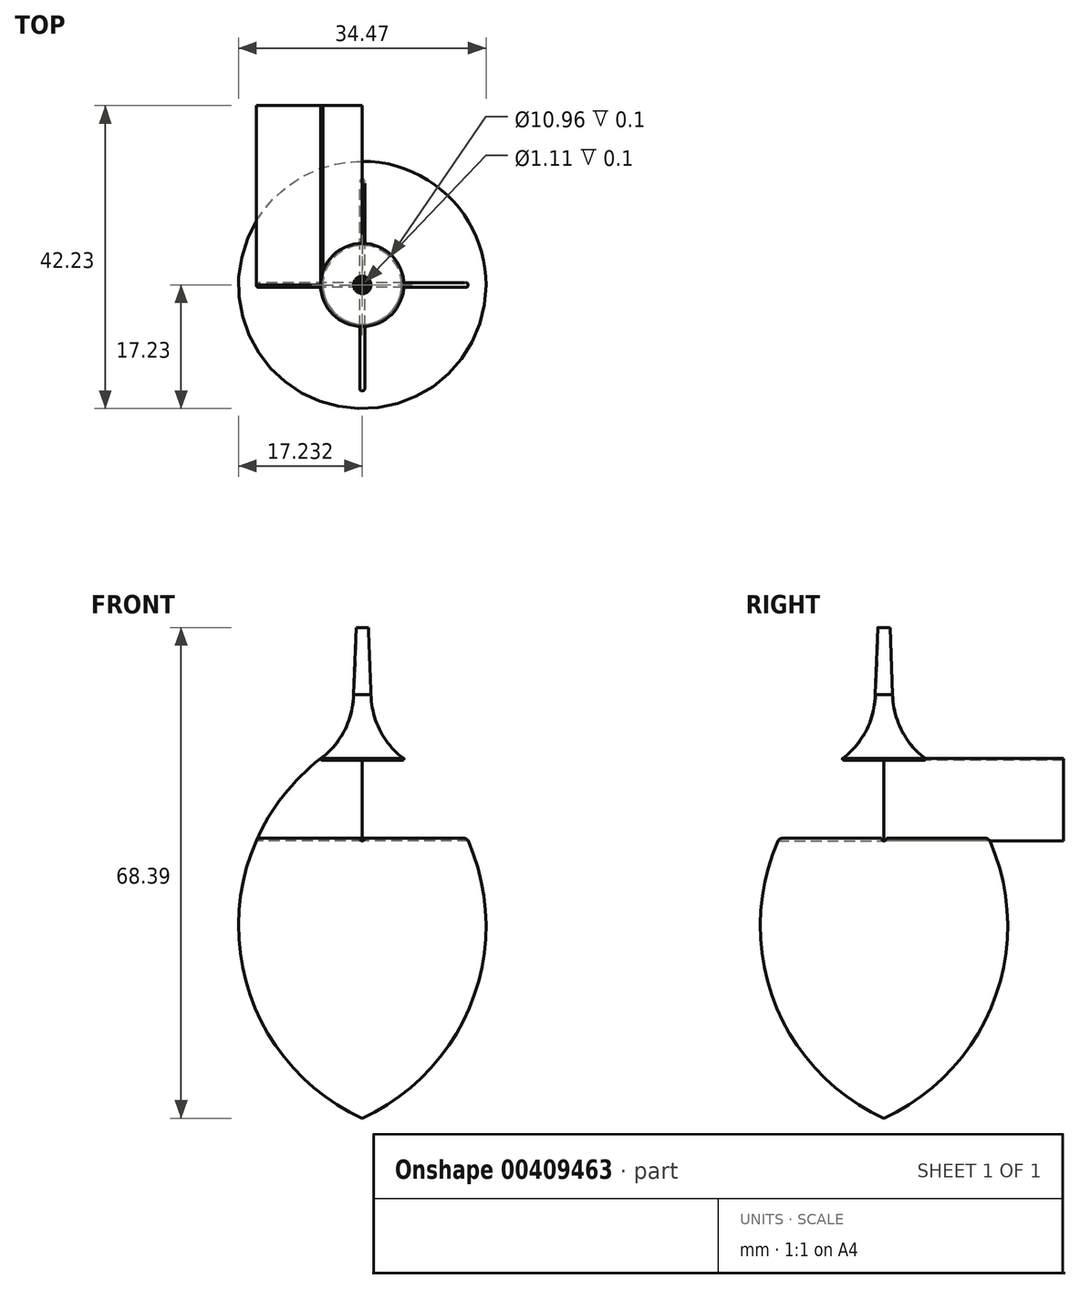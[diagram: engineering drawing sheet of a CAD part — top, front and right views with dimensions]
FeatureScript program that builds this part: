
annotation { "Feature Type Name" : "Feature", "Feature Type Description" : "" }
export const myFeature = defineFeature(function(context is Context, id is Id, definition is map)
    precondition{}
    {
        {
            var Q0;
            Q0=qCreatedBy(makeId("Front.planeOp"),FACE);
            var sketch = newSketch(context, id + "F0", { "sketchPlane" : qUnion([Q0])});
            skLineSegment(sketch, "E0", {"start": v(-71.26, 0) * mm, "end": v(-71.26, 39.03) * mm});
            skLineSegment(sketch, "E1", {"start": v(-71.26, 39.03) * mm, "end": v(-85.85, 39.03) * mm});
            skLineSegment(sketch, "E2", {"start": v(-71.26, 0) * mm, "end": v(-94.3, 0) * mm});
            skArc(sketch, "E3", {"start": v(-85.85, 39.03) * mm, "mid": v(-92.17, 19.97) * mm, "end": v(-94.3, 0) * mm});
            skArc(sketch, "E4", {"start": v(-94.3, 0) * mm, "mid": v(92.17, -19.97) * mm, "end": v(-85.85, 39.03) * mm, "construction": true});
            skLineSegment(sketch, "E5", {"start": v(-71.26, 68.42) * mm, "end": v(-71.26, 50.14) * mm});
            skLineSegment(sketch, "E6", {"start": v(-71.26, 50.14) * mm, "end": v(-77.06, 50.14) * mm, "construction": true});
            skLineSegment(sketch, "E7", {"start": v(-71.26, 68.42) * mm, "end": v(-72.11, 68.42) * mm});
            skLineSegment(sketch, "E8", {"start": v(-72.11, 68.42) * mm, "end": v(-72.47, 59.04) * mm});
            skLineSegment(sketch, "E9", {"start": v(-71.26, 50.14) * mm, "end": v(-71.26, 49.92) * mm});
            skLineSegment(sketch, "E10", {"start": v(-71.26, 49.92) * mm, "end": v(-76.84, 49.92) * mm});
            skArc(sketch, "E11", {"start": v(-72.47, 59.04) * mm, "mid": v(-94.12, 64.58) * mm, "end": v(-77.06, 50.14) * mm, "construction": true});
            skArc(sketch, "E12", {"start": v(-77.06, 50.14) * mm, "mid": v(-73.74, 54.06) * mm, "end": v(-72.47, 59.04) * mm});
            skArc(sketch, "E13", {"start": v(-77.06, 50.14) * mm, "mid": v(-77, 49.99) * mm, "end": v(-76.84, 49.92) * mm});
            skArc(sketch, "E14", {"start": v(-76.84, 49.92) * mm, "mid": v(-76.68, 50.3) * mm, "end": v(-77.06, 50.14) * mm, "construction": true});
            skCircle(sketch, "E15", {"center": v(-59.03, 26.84) * mm, "radius": 29.47 * mm});
            skLineSegment(sketch, "E16", {"start": v(-71.26, 49.92) * mm, "end": v(-71.26, 39.03) * mm});
            skLineSegment(sketch, "E17", {"start": v(-76.84, 49.92) * mm, "end": v(-76.74, 49.92) * mm});
            skLineSegment(sketch, "E18", {"start": v(-76.74, 49.92) * mm, "end": v(-76.74, 50.14) * mm});
            skLineSegment(sketch, "E19", {"start": v(-76.74, 50.14) * mm, "end": v(-71.26, 50.14) * mm});
            skLineSegment(sketch, "E20", {"start": v(-71.26, 39.03) * mm, "end": v(-71.26, 38.69) * mm});
            skLineSegment(sketch, "E21", {"start": v(-71.26, 38.69) * mm, "end": v(-86, 38.69) * mm});
            skSolve(sketch);
        }
        {
            var Q0;
            {var subQ0=sQuery(id+"F0.wireOp",EDGE,"E21");Q0=makeQuery(id+"F0.imprint","IMPRINT",FACE,{"disambiguationData":[TD([[makeQuery(id+"F0.imprint","IMPRINT",EDGE,{"derivedFrom":subQ0}),1.0]])]});}
            var Q1;
            {var subQ0=sQuery(id+"F0.wireOp",EDGE,"E1");Q1=makeQuery(id+"F0.imprint","IMPRINT",FACE,{"disambiguationData":[TD([[makeQuery(id+"F0.imprint","IMPRINT",EDGE,{"derivedFrom":subQ0}),1.0]])]});}
            var Q2;
            Q2=sQuery(id+"F0.wireOp",EDGE,"E0");
            revolve(context, id + "F1", {"entities" : qUnion([Q0, Q1]), "axis" : qUnion([Q2]), "revolveType" : RevolveType.FULL});
        }
        {
            var Q0;
            Q0=makeQuery(id+"F1.opRevolve","SWEPT_FACE",FACE,{"disambiguationData":[OSD([sQuery(id+"F0.wireOp",EDGE,"E1")])]});
            fillet(context, id + "F2", {"entities" : qUnion([Q0]), "radius" : .64 * mm, "tangentPropagation" : true, "allowEdgeOverflow" : false});
        }
        {
            var Q0;
            Q0=makeQuery(id+"F1.opRevolve","SWEPT_FACE",FACE,{"disambiguationData":[OSD([sQuery(id+"F0.wireOp",EDGE,"E1")])]});
            var sketch = newSketch(context, id + "F3", { "sketchPlane" : qUnion([Q0])});
            skLineSegment(sketch, "E22", {"start": v(-71.26, 0) * mm, "end": v(-86.63, 0) * mm});
            skLineSegment(sketch, "E23", {"start": v(-86.63, 0) * mm, "end": v(-86.63, -0.35) * mm});
            skLineSegment(sketch, "E24", {"start": v(-86.63, -0.35) * mm, "end": v(-71.26, -0.35) * mm});
            skLineSegment(sketch, "E25", {"start": v(-71.26, -0.35) * mm, "end": v(-71.26, 0.35) * mm});
            skLineSegment(sketch, "E26", {"start": v(-71.26, 0.35) * mm, "end": v(-86.63, 0.35) * mm});
            skLineSegment(sketch, "E27", {"start": v(-86.63, 0.35) * mm, "end": v(-86.63, 0) * mm});
            skLineSegment(sketch, "E28.1.0", {"start": v(-70.91, -15.37) * mm, "end": v(-70.91, 0) * mm});
            skLineSegment(sketch, "E28.1.1", {"start": v(-71.6, 0) * mm, "end": v(-71.6, -15.37) * mm});
            skLineSegment(sketch, "E28.1.2", {"start": v(-71.26, -15.37) * mm, "end": v(-70.91, -15.37) * mm});
            skLineSegment(sketch, "E28.1.3", {"start": v(-71.6, -15.37) * mm, "end": v(-71.26, -15.37) * mm});
            skLineSegment(sketch, "E28.1.4", {"start": v(-71.26, 0) * mm, "end": v(-71.26, -15.37) * mm});
            skLineSegment(sketch, "E28.1.5", {"start": v(-70.91, 0) * mm, "end": v(-71.6, 0) * mm});
            skLineSegment(sketch, "E28.2.0", {"start": v(-55.88, 0.35) * mm, "end": v(-71.26, 0.35) * mm});
            skLineSegment(sketch, "E28.2.1", {"start": v(-71.26, -0.35) * mm, "end": v(-55.88, -0.35) * mm});
            skLineSegment(sketch, "E28.2.2", {"start": v(-55.88, 0) * mm, "end": v(-55.88, 0.35) * mm});
            skLineSegment(sketch, "E28.2.3", {"start": v(-55.88, -0.35) * mm, "end": v(-55.88, 0) * mm});
            skLineSegment(sketch, "E28.2.4", {"start": v(-71.26, 0) * mm, "end": v(-55.88, 0) * mm});
            skLineSegment(sketch, "E28.2.5", {"start": v(-71.26, 0.35) * mm, "end": v(-71.26, -0.35) * mm});
            skPoint(sketch, "E28.center", {"position": v(-71.26, 0) * mm});
            skLineSegment(sketch, "E29.1.3.0", {"start": v(-71.6, 15.37) * mm, "end": v(-71.6, 0) * mm});
            skLineSegment(sketch, "E29.3.3.0", {"start": v(-70.91, 0) * mm, "end": v(-70.91, 15.37) * mm});
            skLineSegment(sketch, "E29.6.3.0", {"start": v(-71.26, 15.37) * mm, "end": v(-71.6, 15.37) * mm});
            skLineSegment(sketch, "E29.9.3.0", {"start": v(-70.91, 15.37) * mm, "end": v(-71.26, 15.37) * mm});
            skLineSegment(sketch, "E29.12.3.0", {"start": v(-71.26, 0) * mm, "end": v(-71.26, 15.37) * mm});
            skLineSegment(sketch, "E29.15.3.0", {"start": v(-71.6, 0) * mm, "end": v(-70.91, 0) * mm});
            skSolve(sketch);
        }
        {
            var Q0;
            {var subQ0=sQuery(id+"F3.wireOp",EDGE,"E28.1.1");var subQ6=sQuery(id+"F3.wireOp",EDGE,"E24");var subQ7=makeQuery(id+"F3.imprint","INTERSECT",VERTEX,{"derivedFrom":[subQ6,subQ0]});Q0=makeQuery(id+"F3.imprint","IMPRINT",FACE,{"disambiguationData":[TD([[makeQuery(id+"F3.imprint","IMPRINT",EDGE,{"disambiguationData":[TD([[subQ7,1.0]])],"derivedFrom":subQ0}),-1.0]])]});}
            var Q1;
            {var subQ0=sQuery(id+"F3.wireOp",EDGE,"E23");Q1=makeQuery(id+"F3.imprint","IMPRINT",FACE,{"disambiguationData":[TD([[makeQuery(id+"F3.imprint","IMPRINT",EDGE,{"derivedFrom":subQ0}),1.0]])]});}
            var Q2;
            {var subQ0=sQuery(id+"F3.wireOp",EDGE,"E29.3.3.0");var subQ1=sQuery(id+"F3.wireOp",EDGE,"E28.2.0");var subQ2=makeQuery(id+"F3.imprint","INTERSECT",VERTEX,{"derivedFrom":[subQ1,subQ0]});Q2=makeQuery(id+"F3.imprint","IMPRINT",FACE,{"disambiguationData":[TD([[makeQuery(id+"F3.imprint","IMPRINT",EDGE,{"disambiguationData":[TD([[subQ2,1.0]])],"derivedFrom":subQ0}),-1.0]])]});}
            var Q3;
            {var subQ0=sQuery(id+"F3.wireOp",EDGE,"E28.2.2");Q3=makeQuery(id+"F3.imprint","IMPRINT",FACE,{"disambiguationData":[TD([[makeQuery(id+"F3.imprint","IMPRINT",EDGE,{"derivedFrom":subQ0}),1.0]])]});}
            var Q4;
            {var subQ1=sQuery(id+"F3.wireOp",EDGE,"E26");var subQ3=sQuery(id+"F3.wireOp",EDGE,"E29.1.3.0");var subQ4=makeQuery(id+"F3.imprint","INTERSECT",VERTEX,{"derivedFrom":[subQ1,subQ3]});Q4=makeQuery(id+"F3.imprint","IMPRINT",FACE,{"disambiguationData":[TD([[makeQuery(id+"F3.imprint","IMPRINT",EDGE,{"disambiguationData":[TD([[subQ4,1.0]])],"derivedFrom":subQ1}),1.0]])]});}
            var Q5;
            {var subQ1=sQuery(id+"F3.wireOp",EDGE,"E28.2.0");var subQ3=sQuery(id+"F3.wireOp",EDGE,"E29.3.3.0");var subQ4=makeQuery(id+"F3.imprint","INTERSECT",VERTEX,{"derivedFrom":[subQ1,subQ3]});Q5=makeQuery(id+"F3.imprint","IMPRINT",FACE,{"disambiguationData":[TD([[makeQuery(id+"F3.imprint","IMPRINT",EDGE,{"disambiguationData":[TD([[subQ4,-1.0]])],"derivedFrom":subQ1}),1.0]])]});}
            var Q6;
            Q6=sQuery(id+"F3.wireOp",EDGE,"E22");
            revolve(context, id + "F4", {"operationType" : NewBodyOperationType.REMOVE, "entities" : qUnion([Q0, Q1, Q2, Q3, Q4, Q5]), "axis" : qUnion([Q6]), "revolveType" : RevolveType.FULL, "oppositeDirection" : true});
        }
        {
            var Q0;
            {var subQ0=sQuery(id+"F3.wireOp",EDGE,"E28.1.3");Q0=makeQuery(id+"F3.imprint","IMPRINT",FACE,{"disambiguationData":[TD([[makeQuery(id+"F3.imprint","IMPRINT",EDGE,{"derivedFrom":subQ0}),1.0]])]});}
            var Q1;
            {var subQ1=sQuery(id+"F3.wireOp",EDGE,"E24");var subQ3=sQuery(id+"F3.wireOp",EDGE,"E28.1.1");var subQ4=makeQuery(id+"F3.imprint","INTERSECT",VERTEX,{"derivedFrom":[subQ1,subQ3]});Q1=makeQuery(id+"F3.imprint","IMPRINT",FACE,{"disambiguationData":[TD([[makeQuery(id+"F3.imprint","IMPRINT",EDGE,{"disambiguationData":[TD([[subQ4,-1.0]])],"derivedFrom":subQ1}),-1.0]])]});}
            var Q2;
            {var subQ0=sQuery(id+"F3.wireOp",EDGE,"E28.2.5");Q2=makeQuery(id+"F3.imprint","IMPRINT",FACE,{"disambiguationData":[TD([[makeQuery(id+"F3.imprint","IMPRINT",EDGE,{"derivedFrom":subQ0}),-1.0]])]});}
            var Q3;
            {var subQ1=sQuery(id+"F3.wireOp",EDGE,"E26");var subQ3=sQuery(id+"F3.wireOp",EDGE,"E29.1.3.0");var subQ4=makeQuery(id+"F3.imprint","INTERSECT",VERTEX,{"derivedFrom":[subQ1,subQ3]});Q3=makeQuery(id+"F3.imprint","IMPRINT",FACE,{"disambiguationData":[TD([[makeQuery(id+"F3.imprint","IMPRINT",EDGE,{"disambiguationData":[TD([[subQ4,1.0]])],"derivedFrom":subQ1}),1.0]])]});}
            var Q4;
            {var subQ1=sQuery(id+"F3.wireOp",EDGE,"E26");var subQ3=sQuery(id+"F3.wireOp",EDGE,"E29.1.3.0");var subQ4=makeQuery(id+"F3.imprint","INTERSECT",VERTEX,{"derivedFrom":[subQ1,subQ3]});Q4=makeQuery(id+"F3.imprint","IMPRINT",FACE,{"disambiguationData":[TD([[makeQuery(id+"F3.imprint","IMPRINT",EDGE,{"disambiguationData":[TD([[subQ4,1.0]])],"derivedFrom":subQ1}),-1.0]])]});}
            var Q5;
            {var subQ0=sQuery(id+"F3.wireOp",EDGE,"E29.6.3.0");Q5=makeQuery(id+"F3.imprint","IMPRINT",FACE,{"disambiguationData":[TD([[makeQuery(id+"F3.imprint","IMPRINT",EDGE,{"derivedFrom":subQ0}),1.0]])]});}
            var Q6;
            Q6=sQuery(id+"F3.wireOp",EDGE,"E29.12.3.0");
            revolve(context, id + "F5", {"operationType" : NewBodyOperationType.REMOVE, "entities" : qUnion([Q0, Q1, Q2, Q3, Q4, Q5]), "axis" : qUnion([Q6]), "revolveType" : RevolveType.FULL, "oppositeDirection" : true});
        }
        {
            var Q0;
            {var subQ4=sQuery(id+"F0.wireOp",EDGE,"E7");Q0=makeQuery(id+"F0.imprint","IMPRINT",FACE,{"disambiguationData":[TD([[makeQuery(id+"F0.imprint","IMPRINT",EDGE,{"derivedFrom":subQ4}),1.0]])]});}
            var Q1;
            {var subQ5=sQuery(id+"F0.wireOp",EDGE,"E13");Q1=makeQuery(id+"F0.imprint","IMPRINT",FACE,{"disambiguationData":[TD([[makeQuery(id+"F0.imprint","IMPRINT",EDGE,{"derivedFrom":subQ5}),1.0]])]});}
            var Q2;
            Q2=makeQuery(id+"F0.imprint","IMPRINT",FACE,{"disambiguationData":[TD([[makeQuery(id+"F0.imprint","IMPRINT",EDGE,{"derivedFrom":sQuery(id+"F0.wireOp",EDGE,"E9")}),-1.0]])]});
            var Q3;
            Q3=sQuery(id+"F0.wireOp",EDGE,"E5");
            revolve(context, id + "F6", {"entities" : qUnion([Q0, Q1, Q2]), "axis" : qUnion([Q3]), "revolveType" : RevolveType.FULL});
        }
        {
            var Q0;
            Q0=makeQuery(id+"F6.opRevolve","SWEPT_FACE",FACE,{"disambiguationData":[OSD([sQuery(id+"F0.wireOp",EDGE,"E12")])]});
            var Q1;
            Q1=makeQuery(id+"F6.opRevolve","SWEPT_BODY",BODY,{"disambiguationData":[OSD([sQuery(id+"F0.wireOp",EDGE,"E5"),sQuery(id+"F0.wireOp",EDGE,"E7"),sQuery(id+"F0.wireOp",EDGE,"E8"),sQuery(id+"F0.wireOp",EDGE,"E9"),sQuery(id+"F0.wireOp",EDGE,"E10"),sQuery(id+"F0.wireOp",EDGE,"E12"),sQuery(id+"F0.wireOp",EDGE,"E13")])]});
            shell(context, id + "F7", {"isHollow" : true, "entities" : qUnion([Q0]), "parts" : qUnion([Q1]), "thickness" : 0.1 * mm});
        }
        {
            var Q0;
            Q0=makeQuery(id+"F6.opRevolve","SWEPT_FACE",FACE,{"disambiguationData":[OSD([sQuery(id+"F0.wireOp",EDGE,"E10")])]});
            var sketch = newSketch(context, id + "F8", { "sketchPlane" : qUnion([Q0])});
            skCircle(sketch, "E30.0", {"center": v(-71.26, 0) * mm, "radius": 5.48 * mm});
            skSolve(sketch);
        }
        {
            var Q0;
            Q0=makeQuery(id+"F8.imprint","IMPRINT",FACE,{"disambiguationData":[TD([[makeQuery(id+"F8.imprint","IMPRINT",EDGE,{"derivedFrom":sQuery(id+"F8.wireOp",EDGE,"E30.0")}),1.0]])]});
            extrude(context, id + "F9", {"entities" : qUnion([Q0]), "operationType" : NewBodyOperationType.REMOVE, "oppositeDirection" : true, "depth" : .2 * mm});
        }
        {
            var Q0;
            Q0=makeQuery(id+"F6.opRevolve","SWEPT_FACE",FACE,{"disambiguationData":[OSD([sQuery(id+"F0.wireOp",EDGE,"E7")])]});
            var sketch = newSketch(context, id + "F10", { "sketchPlane" : qUnion([Q0])});
            skCircle(sketch, "E31.0", {"center": v(-71.26, 0) * mm, "radius": 0.55 * mm});
            skSolve(sketch);
        }
        {
            var Q0;
            Q0=makeQuery(id+"F10.imprint","IMPRINT",FACE,{"disambiguationData":[TD([[makeQuery(id+"F10.imprint","IMPRINT",EDGE,{"derivedFrom":sQuery(id+"F10.wireOp",EDGE,"E31.0")}),1.0]])]});
            extrude(context, id + "F11", {"entities" : qUnion([Q0]), "operationType" : NewBodyOperationType.REMOVE, "oppositeDirection" : true, "depth" : 25 * mm});
        }
        {
            var Q0;
            {var subQ1=sQuery(id+"F0.wireOp",EDGE,"E1");Q0=makeQuery(id+"F0.imprint","IMPRINT",FACE,{"disambiguationData":[TD([[makeQuery(id+"F0.imprint","IMPRINT",EDGE,{"derivedFrom":subQ1}),-1.0]])]});}
            var Q1;
            {var subQ0=sQuery(id+"F0.wireOp",EDGE,"E1");Q1=makeQuery(id+"F0.imprint","IMPRINT",FACE,{"disambiguationData":[TD([[makeQuery(id+"F0.imprint","IMPRINT",EDGE,{"derivedFrom":subQ0}),1.0]])]});}
            var Q2;
            Q2=makeQuery(id+"F0.imprint","IMPRINT",FACE,{"disambiguationData":[TD([[makeQuery(id+"F0.imprint","IMPRINT",EDGE,{"derivedFrom":sQuery(id+"F0.wireOp",EDGE,"E9")}),-1.0]])]});
            extrude(context, id + "F12", {"entities" : qUnion([Q0, Q1, Q2]), "oppositeDirection" : true, "depth" : 25 * mm});
        }
    });
